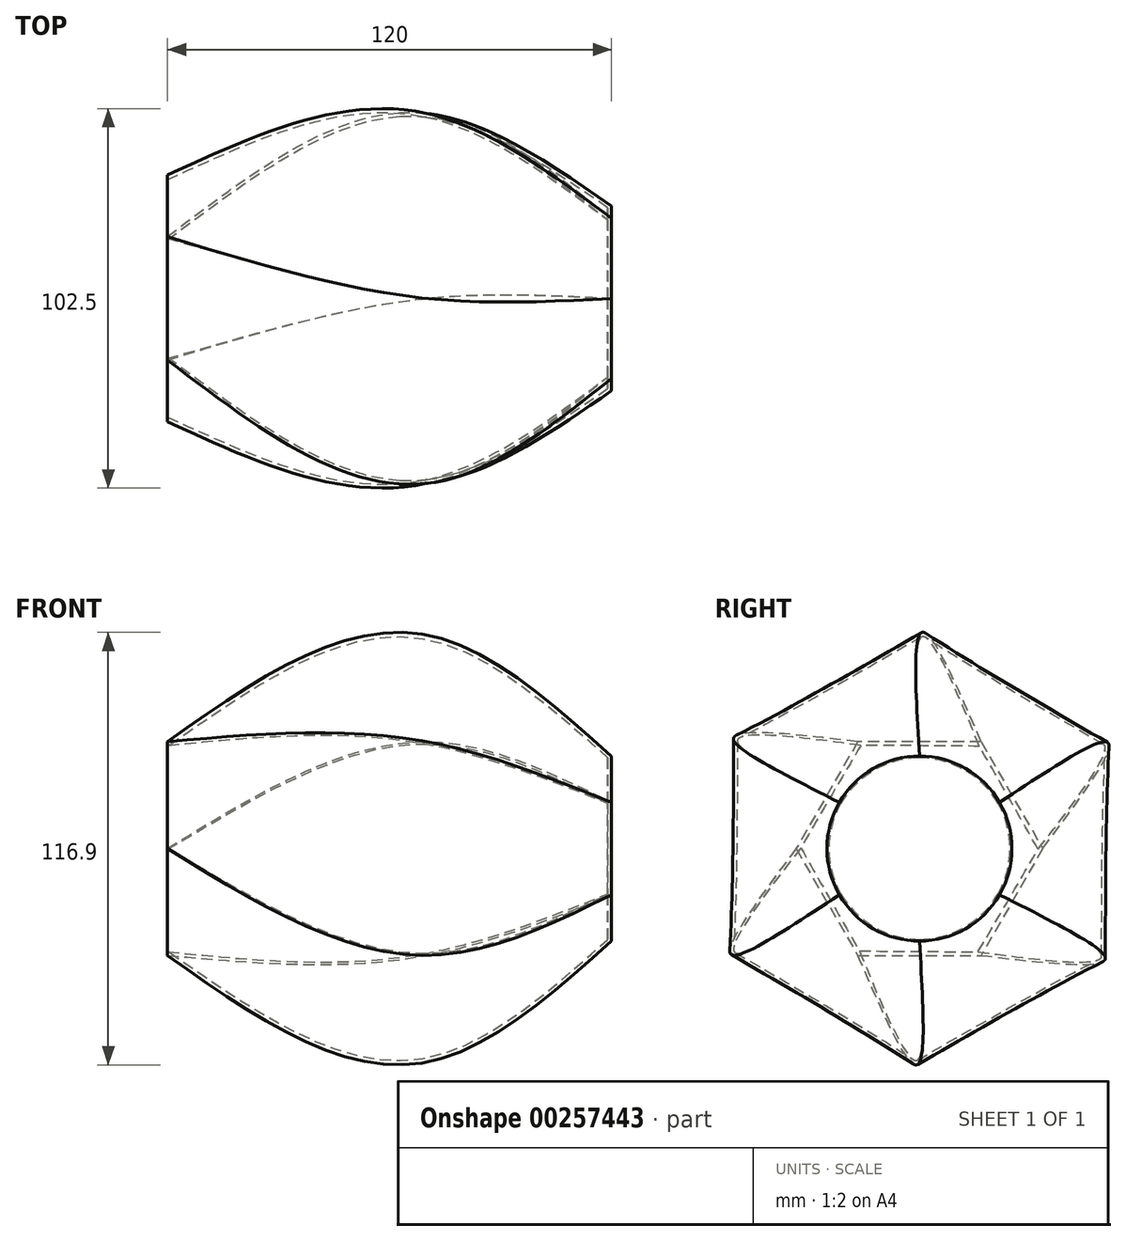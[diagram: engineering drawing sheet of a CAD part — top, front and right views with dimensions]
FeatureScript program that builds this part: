
annotation { "Feature Type Name" : "Feature", "Feature Type Description" : "" }
export const myFeature = defineFeature(function(context is Context, id is Id, definition is map)
    precondition{}
    {
        {
            var Q0;
            Q0=qCreatedBy(makeId("Right.planeOp"),FACE);
            var sketch = newSketch(context, id + "F0", { "sketchPlane" : qUnion([Q0])});
            skCircle(sketch, "E0", {"center": v(0, 0) * mm, "radius": 25 * mm});
            skSolve(sketch);
        }
        {
            var Q0;
            Q0=qCreatedBy(makeId("Right.planeOp"),FACE);
            cPlane(context, id + "F1", {"entities" : qUnion([Q0]), "cplaneType" : CPlaneType.OFFSET, "offset" : 50 * mm, "oppositeDirection" : true, "width" : 150 * mm, "height" : 150 * mm});
        }
        {
            var Q0;
            Q0=qCreatedBy(makeId("Right.planeOp"),FACE);
            cPlane(context, id + "F2", {"entities" : qUnion([Q0]), "cplaneType" : CPlaneType.OFFSET, "offset" : 120 * mm, "oppositeDirection" : true, "width" : 150 * mm, "height" : 150 * mm});
        }
        {
            var Q0;
            Q0=qCreatedBy(id+"F1.planeOp",FACE);
            var sketch = newSketch(context, id + "F3", { "sketchPlane" : qUnion([Q0])});
            skLineSegment(sketch, "E1.0", {"start": v(50, 28.87) * mm, "end": v(50, -28.87) * mm});
            skLineSegment(sketch, "E1.1", {"start": v(50, -28.87) * mm, "end": v(0, -57.74) * mm});
            skLineSegment(sketch, "E1.2", {"start": v(0, -57.74) * mm, "end": v(-50, -28.87) * mm});
            skLineSegment(sketch, "E1.3", {"start": v(-50, -28.87) * mm, "end": v(-50, 28.87) * mm});
            skLineSegment(sketch, "E1.4", {"start": v(-50, 28.87) * mm, "end": v(0, 57.74) * mm});
            skLineSegment(sketch, "E1.5", {"start": v(0, 57.74) * mm, "end": v(50, 28.87) * mm});
            skPoint(sketch, "E1.0.midPoint", {"position": v(50, 0) * mm});
            skSolve(sketch);
        }
        {
            var Q0;
            Q0=qCreatedBy(id+"F2.planeOp",FACE);
            var sketch = newSketch(context, id + "F4", { "sketchPlane" : qUnion([Q0])});
            skLineSegment(sketch, "E2", {"start": v(16.67, 28.87) * mm, "end": v(-16.67, 28.87) * mm});
            skLineSegment(sketch, "E3", {"start": v(-16.67, 28.87) * mm, "end": v(-33.33, 0) * mm});
            skLineSegment(sketch, "E4", {"start": v(16.67, 28.87) * mm, "end": v(33.33, 0) * mm});
            skLineSegment(sketch, "E5", {"start": v(33.33, 0) * mm, "end": v(16.67, -28.87) * mm});
            skLineSegment(sketch, "E6", {"start": v(-33.33, 0) * mm, "end": v(-16.67, -28.87) * mm});
            skLineSegment(sketch, "E7", {"start": v(-16.67, -28.87) * mm, "end": v(16.67, -28.87) * mm});
            skSolve(sketch);
        }
        {
            var Q0;
            Q0=makeQuery(id+"F4.imprint","IMPRINT",FACE,{"disambiguationData":[TD([[makeQuery(id+"F4.imprint","IMPRINT",EDGE,{"derivedFrom":sQuery(id+"F4.wireOp",EDGE,"E2")}),1.0]])]});
            var Q1;
            Q1=makeQuery(id+"F3.imprint","IMPRINT",FACE,{"disambiguationData":[TD([[makeQuery(id+"F3.imprint","IMPRINT",EDGE,{"derivedFrom":sQuery(id+"F3.wireOp",EDGE,"E1.0")}),-1.0]])]});
            var Q2;
            Q2=makeQuery(id+"F0.imprint","IMPRINT",FACE,{"disambiguationData":[TD([[makeQuery(id+"F0.imprint","IMPRINT",EDGE,{"derivedFrom":sQuery(id+"F0.wireOp",EDGE,"E0")}),1.0]])]});
            loft(context, id + "F5", {"sheetProfilesArray" : [{ "sheetProfileEntities" : qUnion([Q0]) }, { "sheetProfileEntities" : qUnion([Q1]) }, { "sheetProfileEntities" : qUnion([Q2]) }]});
        }
        {
            var Q0;
            Q0=makeQuery(id+"F5.opLoft","CAP_FACE",FACE,{"disambiguationData":[OSD([makeQuery(id+"F4.imprint","IMPRINT",FACE,{"disambiguationData":[TD([[makeQuery(id+"F4.imprint","IMPRINT",EDGE,{"derivedFrom":sQuery(id+"F4.wireOp",EDGE,"E2")}),1.0]])]})])],"isStart":true});
            shell(context, id + "F6", {"entities" : qUnion([Q0]), "thickness" : 1 * mm});
        }
    });
